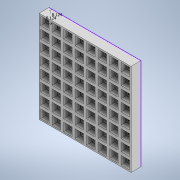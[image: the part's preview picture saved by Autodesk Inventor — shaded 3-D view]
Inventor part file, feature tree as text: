
AUTODESK INVENTOR PART (.ipt)
format: ipt  version: 2020.1 (Build 241239000, 239)  size: 1,367,552 bytes
history: native  units: in
note: dims shown in document units (in); Inventor stores cm internally (conversion verified against a paired STEP export)
features: extrude x4, sketch x2
ambient origin geometry x8: Origin, YZ Plane, XZ Plane, XY Plane, X Axis, Y Axis, Z Axis, Center Point
bodies: Solid1 (feature_tree)
feature tree (6):
  sketch  "Sketch1"  dims[d34=0.2756in d35=0.0in d47=0.1378in d48=0.0in]
  extrude  "Extrusion1"  Depth=0.1378in TaperAngle=0.0deg
  extrude  "Extrusion2"  Depth=0.3198in
  extrude  "Extrusion4"  Depth=0.3198in
  extrude  "Extrusion6"  Depth=0.0197in TaperAngle=0.0deg
  sketch  "Sketch3"  dims[d51=0.0984in d52=0.0in d68=3.1496in d70=0.3198in d71=3.1496in d73=0.3198in d77=3.1496in d79=0.3198in d80=3.1496in d82=0.3198in d85=0.3937in d86=0.0in d36=0.0197in d37=0.0344in]
